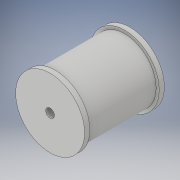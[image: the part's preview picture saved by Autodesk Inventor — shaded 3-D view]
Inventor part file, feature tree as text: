
AUTODESK INVENTOR PART (.ipt)
format: ipt  version: 2019 (Build 230136000, 136)  size: 124,416 bytes
history: native  units: mm
features: sketch x4, extrude x3, other x1, hole x1
ambient origin geometry x8: Origin, YZ Plane, XZ Plane, XY Plane, X Axis, Y Axis, Z Axis, Center Point
bodies: Body1 (feature_tree)
feature tree (9):
  other  "ソリッド1"
  extrude  "押し出し1"  Depth=36.26mm
  extrude  "押し出し2"  Depth=40.0mm TaperAngle=0.0deg
  extrude  "押し出し3"  Depth=39.76mm
  hole  "穴1"  [1 undecoded]
  sketch  "スケッチ1"
  sketch  "スケッチ2"
  sketch  "スケッチ3"
  sketch  "スケッチ4"
note: 1 required parameter value undecoded (feature->parameter linkage not recoverable at this tier; creation-order binding heuristic only, values carry confidence <= 0.55)
